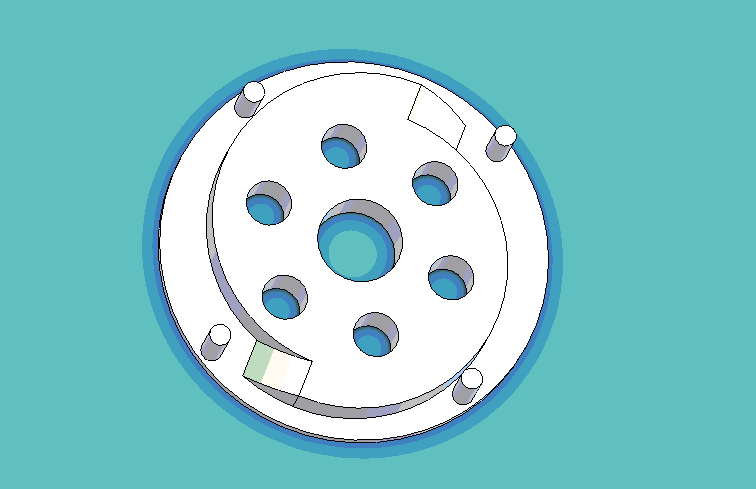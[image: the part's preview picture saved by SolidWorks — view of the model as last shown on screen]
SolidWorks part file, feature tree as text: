
SOLIDWORKS PART (.sldprt)
format: sldprt  version: not decoded by parser v0  size: 352,256 bytes
history: native  units: mm
features: sketch x10, extrude x5, plane x4, cut_extrude x4, pattern_circular x2, material x1 (+10 scaffold rows collapsed)
feature tree (36):
  scaffold x10  (default folders/planes/origin — collapsed)
  material  "Material <not specified>"
  plane  "Frontal"
  plane  "Horizontal"
  plane  "Profile"
  sketch  "Sketch1"  dims[D1=~57.707125mm]
  extrude  "Extrude1"  Depth=3.302mm
  sketch  "Sketch2"  dims[D1=~17.051268mm]
  sketch  "Sketch4"  dims[D1=~51.651405mm]
  extrude  "Extrude2"  Depth=12.446mm
  sketch  "Sketch5"
  cut_extrude  "Cut-Extrude3"  [1 undecoded]
  sketch  "Sketch7"  dims[D1=32.512mm]
  cut_extrude  "Cut-Extrude4"  [1 undecoded]
  pattern_circular  "CirPattern1"  Count=6 Angle=360deg
  plane  "Plane1"
  sketch  "Sketch18"  dims[D1=71.882mm D2=18.796mm]
  extrude  "Extrude3"  [1 undecoded]
  sketch  "Sketch19"
  cut_extrude  "Cut-Extrude5"  Depth=12.446mm
  sketch  "Sketch20"  dims[D1=71.882mm D2=18.796mm]
  extrude  "Extrude4"  [1 undecoded]
  sketch  "Sketch21"
  cut_extrude  "Cut-Extrude6"  Depth=12.446mm
  sketch  "Sketch22"  dims[c1.D1=117.856mm c1.D3=~3.697232mm c1.D2=~93.598172mm c2.D2=32.0deg]
  extrude  "Extrude5"  Depth=18.542mm
  pattern_circular  "CirPattern2"  Count=4 Angle=360deg
decode coverage: 14 of 21 modeling features carry decoded parameters
note: ~ marks probable driven/reference dimensions
note: 4 parameter values undecoded
summary: no parameter record found for 4 features
note: suppression state not decoded; provenance and decode notes live in map.json
